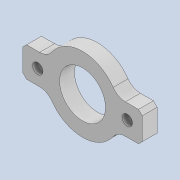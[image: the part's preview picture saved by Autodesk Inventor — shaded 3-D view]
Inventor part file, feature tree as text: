
AUTODESK INVENTOR PART (.ipt)
format: ipt  version: 2020 (Build 240168000, 168)  size: 140,288 bytes
history: native  units: mm
features: thicken_offset x5, sketch x3, other x3, extrude x2, hole x1, chamfer x1, fillet x1, reference x1
ambient origin geometry x8: Origin, YZ Plane, XZ Plane, XY Plane, X Axis, Y Axis, Z Axis, Center Point
bodies: Solid1 (feature_tree)
feature tree (17):
  extrude  "Extrusion1"  Depth=4.0mm
  hole  "Hole1"  [1 undecoded]
  extrude  "Extrusion2"  Depth=2.0mm
  thicken_offset  "Thicken1"
  thicken_offset  "Thicken2"
  chamfer  "Chamfer1"  Distance=2.0mm
  fillet  "Fillet1"  Radius=0.5mm
  thicken_offset  "Thicken3"
  thicken_offset  "Thicken4"
  thicken_offset  "Thicken5"
  sketch  "Sketch1"  dims[d0=10.0mm d1=4.0mm]
  sketch  "Sketch2"  dims[d2=17.0mm d3=2.0mm d4=0.0mm]
  reference  "Reference1"
  sketch  "Sketch3"  dims[d5=1.6mm d6=6.0mm d7=4.0mm d8=2.0mm d9=90.0deg d10=8.0mm d11=20.594885mm d12=6.0mm d13=2.0mm d14=0.0mm d15=0.5mm d16=0.5mm d17=0.5mm d18=0.5mm d19=0.5mm d20=2.0mm d21=45.0deg d22=2.0mm d23=0.08mm d24=0.08mm d25=0.1mm d26=0.1mm d27=0.1mm d28=0.1mm]
  parser-record x1  (decoder bookkeeping rows leaked as tree rows — omitted from the tree; the rows remain in map.json)
  other  "tip2_ass_t1.iam"
  other  "cable_holder_1:1"
note: 1 required parameter value undecoded (feature->parameter linkage not recoverable at this tier; creation-order binding heuristic only, values carry confidence <= 0.55)
note: 1 file-system path scrubbed to <path> (originals preserved in map.json)
